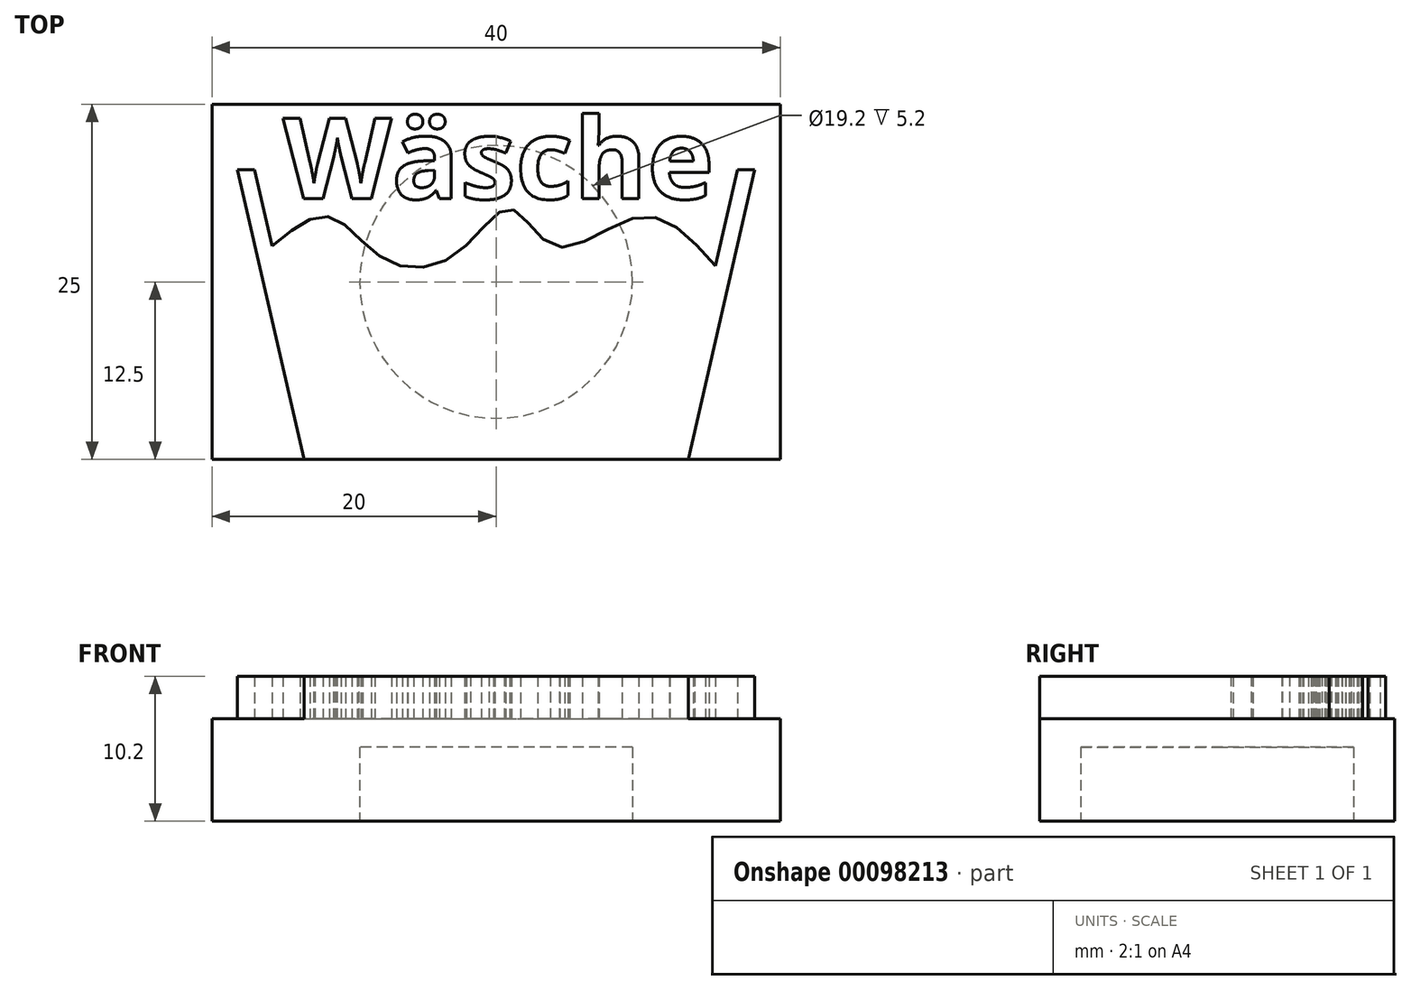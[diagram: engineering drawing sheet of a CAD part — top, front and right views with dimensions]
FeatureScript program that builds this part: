
annotation { "Feature Type Name" : "Feature", "Feature Type Description" : "" }
export const myFeature = defineFeature(function(context is Context, id is Id, definition is map)
    precondition{}
    {
        {
            var Q0;
            Q0=qCreatedBy(makeId("Top.planeOp"),FACE);
            var sketch = newSketch(context, id + "F0", { "sketchPlane" : qUnion([Q0])});
            skCircle(sketch, "E0", {"center": v(0, 0) * mm, "radius": 9.6 * mm});
            skCircle(sketch, "E1.0", {"center": v(0, 0) * mm, "radius": 11.6 * mm});
            skSolve(sketch);
        }
        {
            var Q0;
            Q0=qSketchRegion(id+"F0",true);
            extrude(context, id + "F1", {"entities" : qUnion([Q0]), "depth" : 5.2 * mm});
        }
        {
            var Q0;
            Q0=makeQuery(id+"F1.opExtrude","CAP_FACE",FACE,{"disambiguationData":[OSD([sQuery(id+"F0.wireOp",EDGE,"E0"),sQuery(id+"F0.wireOp",EDGE,"E1.0")])],"isStart":false});
            var sketch = newSketch(context, id + "F2", { "sketchPlane" : qUnion([Q0])});
            skSolve(sketch);
        }
        {
            var Q0;
            Q0=makeQuery(id+"F2.imprint","IMPRINT",FACE,{"disambiguationData":[TD([[makeQuery(id+"F2.imprint","IMPRINT",EDGE,{"derivedFrom":makeQuery(id+"F1.opExtrude","CAP_EDGE",EDGE,{"disambiguationData":[OSD([sQuery(id+"F0.wireOp",EDGE,"E0")])],"isStart":false})}),1.0]])]});
            var Q1;
            Q1=makeQuery(id+"F2.imprint","IMPRINT",FACE,{"disambiguationData":[TD([[makeQuery(id+"F2.imprint","IMPRINT",EDGE,{"derivedFrom":makeQuery(id+"F1.opExtrude","CAP_EDGE",EDGE,{"disambiguationData":[OSD([sQuery(id+"F0.wireOp",EDGE,"E0")])],"isStart":false})}),-1.0]])]});
            extrude(context, id + "F3", {"entities" : qUnion([Q0, Q1]), "operationType" : NewBodyOperationType.ADD, "depth" : 2 * mm});
        }
        {
            var Q0;
            Q0=makeQuery(id+"F3.opExtrude","CAP_FACE",FACE,{"disambiguationData":[OSD([sQuery(id+"F0.wireOp",EDGE,"E1.0")])],"isStart":false});
            var sketch = newSketch(context, id + "F4", { "sketchPlane" : qUnion([Q0])});
            skLineSegment(sketch, "E2.bottom", {"start": v(-20, 12.5) * mm, "end": v(20, 12.5) * mm});
            skLineSegment(sketch, "E2.top", {"start": v(-20, -12.5) * mm, "end": v(20, -12.5) * mm});
            skLineSegment(sketch, "E2.left", {"start": v(-20, 12.5) * mm, "end": v(-20, -12.5) * mm});
            skLineSegment(sketch, "E2.right", {"start": v(20, 12.5) * mm, "end": v(20, -12.5) * mm});
            skPoint(sketch, "E2.middle", {"position": v(0, 0) * mm});
            skSolve(sketch);
        }
        {
            var Q0;
            Q0=makeQuery(id+"F4.imprint","IMPRINT",FACE,{"disambiguationData":[TD([[makeQuery(id+"F4.imprint","IMPRINT",EDGE,{"derivedFrom":sQuery(id+"F4.wireOp",EDGE,"E2.bottom")}),-1.0]])]});
            extrude(context, id + "F5", {"entities" : qUnion([Q0]), "operationType" : NewBodyOperationType.ADD, "oppositeDirection" : true, "depth" : 7.2 * mm});
        }
        {
            var Q0;
            {var subQ0=sQuery(id+"F0.wireOp",EDGE,"E1.0");Q0=makeQuery(id+"F5.boolean.opBoolean","MERGE",FACE,{"derivedFrom":[makeQuery(id+"F3.opExtrude","CAP_FACE",FACE,{"disambiguationData":[OSD([subQ0])],"isStart":false}),makeQuery(id+"F5.opExtrude","CAP_FACE",FACE,{"disambiguationData":[OSD([subQ0,sQuery(id+"F4.wireOp",EDGE,"E2.bottom"),sQuery(id+"F4.wireOp",EDGE,"E2.top"),sQuery(id+"F4.wireOp",EDGE,"E2.left"),sQuery(id+"F4.wireOp",EDGE,"E2.right")])],"isStart":true})]});}
            var sketch = newSketch(context, id + "F6", { "sketchPlane" : qUnion([Q0])});
            skLineSegment(sketch, "E3", {"start": v(-17, 7.89) * mm, "end": v(-12.82, -10.3) * mm});
            skLineSegment(sketch, "E4", {"start": v(-12.82, -10.3) * mm, "end": v(12.82, -10.3) * mm});
            skLineSegment(sketch, "E5", {"start": v(12.82, -10.3) * mm, "end": v(17, 7.89) * mm});
            skFitSpline(sketch, "E6", {"points": [v(-15.77, 2.52) * mm, v(-11.76, 4.6) * mm, v(-7.75, 1.54) * mm, v(-2.67, 2.08) * mm, v(1, 5.13) * mm, v(4.25, 2.49) * mm, v(10.23, 4.6) * mm, v(15.45, 1.13) * mm], "startDerivative": vector(31.07, 26.29) * mm, "endDerivative": vector(30.95, -35.02) * mm});
            skLineSegment(sketch, "E7", {"start": v(-17, 7.89) * mm, "end": v(-18.2, 7.89) * mm});
            skLineSegment(sketch, "E8", {"start": v(-18.2, 7.89) * mm, "end": v(-13.52, -12.5) * mm});
            skLineSegment(sketch, "E9", {"start": v(17, 7.89) * mm, "end": v(18.2, 7.89) * mm});
            skLineSegment(sketch, "E10", {"start": v(18.2, 7.89) * mm, "end": v(13.52, -12.5) * mm});
            skSolve(sketch);
        }
        {
            var Q0;
            {var subQ0=sQuery(id+"F6.wireOp",EDGE,"E4");Q0=makeQuery(id+"F6.imprint","IMPRINT",FACE,{"disambiguationData":[TD([[makeQuery(id+"F6.imprint","IMPRINT",EDGE,{"derivedFrom":subQ0}),1.0]])]});}
            var Q1;
            {var subQ1=sQuery(id+"F6.wireOp",EDGE,"E4");Q1=makeQuery(id+"F6.imprint","IMPRINT",FACE,{"disambiguationData":[TD([[makeQuery(id+"F6.imprint","IMPRINT",EDGE,{"derivedFrom":subQ1}),-1.0]])]});}
            extrude(context, id + "F7", {"entities" : qUnion([Q0, Q1]), "operationType" : NewBodyOperationType.ADD, "depth" : 3 * mm});
        }
        {
            var Q0;
            {var subQ0=sQuery(id+"F0.wireOp",EDGE,"E1.0");Q0=makeQuery(id+"F5.boolean.opBoolean","MERGE",FACE,{"derivedFrom":[makeQuery(id+"F3.opExtrude","CAP_FACE",FACE,{"disambiguationData":[OSD([subQ0])],"isStart":false}),makeQuery(id+"F5.opExtrude","CAP_FACE",FACE,{"disambiguationData":[OSD([subQ0,sQuery(id+"F4.wireOp",EDGE,"E2.bottom"),sQuery(id+"F4.wireOp",EDGE,"E2.top"),sQuery(id+"F4.wireOp",EDGE,"E2.left"),sQuery(id+"F4.wireOp",EDGE,"E2.right")])],"isStart":true})]});}
            var sketch = newSketch(context, id + "F8", { "sketchPlane" : qUnion([Q0])});
            skText(sketch, "E11", { "text": "Wäsche", "fontName": "OpenSans-Bold.ttf"});
            const initialGuessF8  = {"E11": [-0.015, 0.00585, 1, 0, 0.0057]};
            skSetInitialGuess(sketch, initialGuessF8);
            skSolve(sketch);
        }
        {
            var Q0;
            Q0 = qSketchRegion(id + "F8", true);
            extrude(context, id + "F9", {"entities" : qUnion([Q0]), "operationType" : NewBodyOperationType.ADD, "depth" : 3 * mm});
        }
    });
